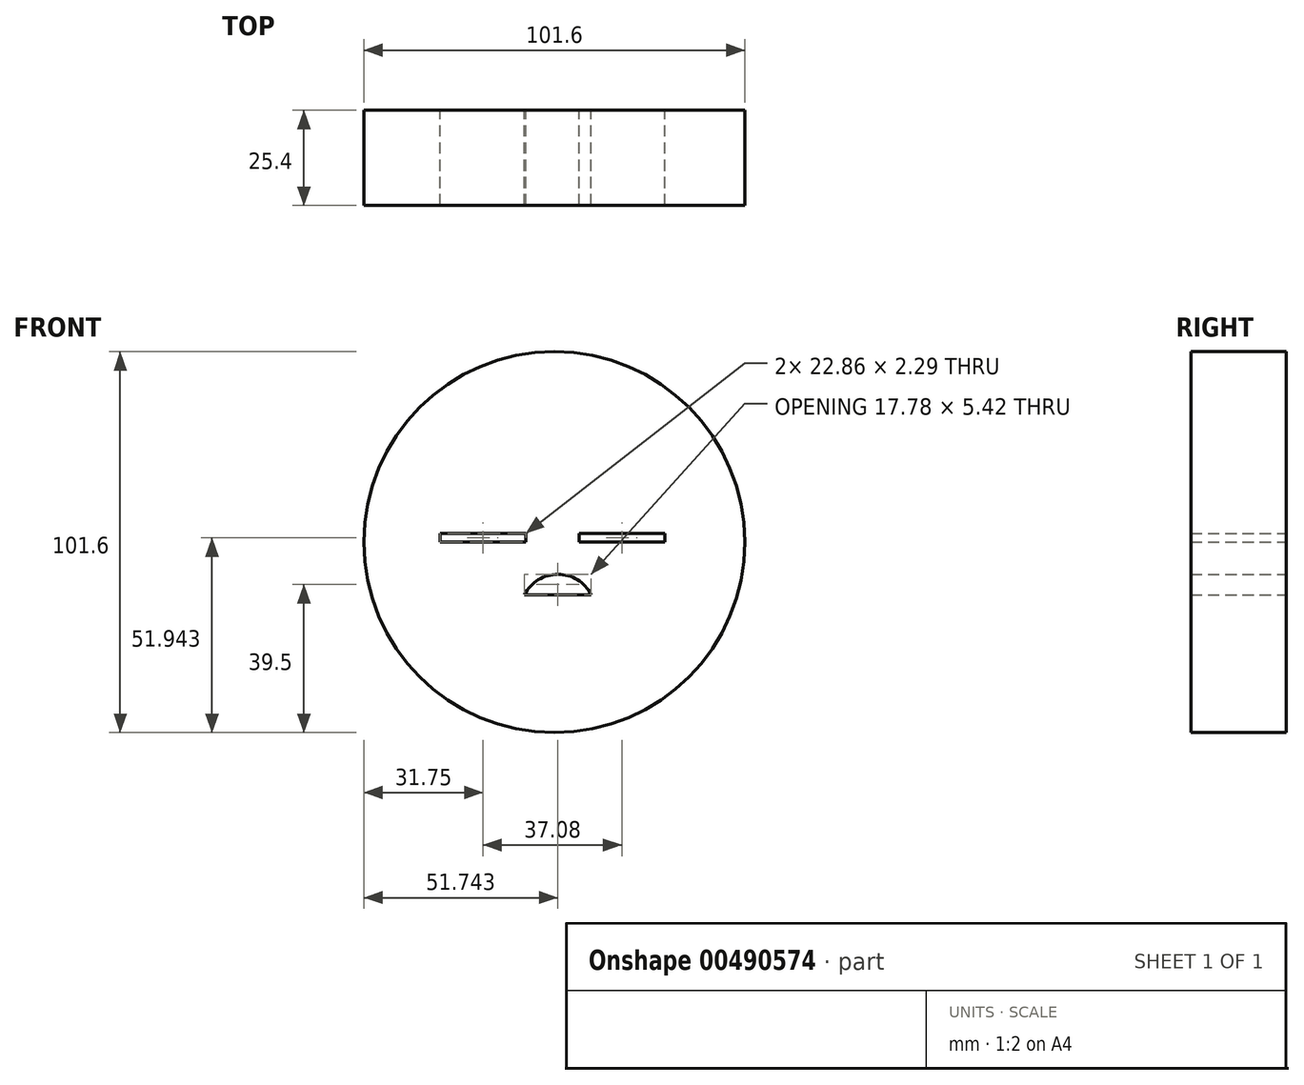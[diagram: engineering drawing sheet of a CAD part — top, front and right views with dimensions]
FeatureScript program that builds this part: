
annotation { "Feature Type Name" : "Feature", "Feature Type Description" : "" }
export const myFeature = defineFeature(function(context is Context, id is Id, definition is map)
    precondition{}
    {
        {
            var Q0;
            Q0=qCreatedBy(makeId("Front.planeOp"),FACE);
            var sketch = newSketch(context, id + "F0", { "sketchPlane" : qUnion([Q0])});
            skCircle(sketch, "E0", {"center": v(0, 0) * mm, "radius": 50.8 * mm});
            skLineSegment(sketch, "E1.bottom", {"start": v(-30.48, 0) * mm, "end": v(-7.62, 0) * mm});
            skLineSegment(sketch, "E1.top", {"start": v(-30.48, 2.29) * mm, "end": v(-7.62, 2.29) * mm});
            skLineSegment(sketch, "E1.left", {"start": v(-30.48, 0) * mm, "end": v(-30.48, 2.29) * mm});
            skLineSegment(sketch, "E1.right", {"start": v(-7.62, 0) * mm, "end": v(-7.62, 2.29) * mm});
            skLineSegment(sketch, "E2.bottom", {"start": v(6.6, 0) * mm, "end": v(29.46, 0) * mm});
            skLineSegment(sketch, "E2.top", {"start": v(6.6, 2.29) * mm, "end": v(29.46, 2.29) * mm});
            skLineSegment(sketch, "E2.left", {"start": v(6.6, 0) * mm, "end": v(6.6, 2.29) * mm});
            skLineSegment(sketch, "E2.right", {"start": v(29.46, 0) * mm, "end": v(29.46, 2.29) * mm});
            skLineSegment(sketch, "E3", {"start": v(-7.95, -14.01) * mm, "end": v(9.83, -14.01) * mm});
            skArc(sketch, "E4", {"start": v(9.83, -14.01) * mm, "mid": v(0.94, -8.59) * mm, "end": v(-7.95, -14.01) * mm});
            skSolve(sketch);
        }
        {
            var Q0;
            Q0=makeQuery(id+"F0.imprint","IMPRINT",FACE,{"disambiguationData":[TD([[makeQuery(id+"F0.imprint","IMPRINT",EDGE,{"derivedFrom":sQuery(id+"F0.wireOp",EDGE,"E0")}),1.0]])]});
            extrude(context, id + "F1", {"entities" : qUnion([Q0]), "depth" : 25.4 * mm});
        }
    });
